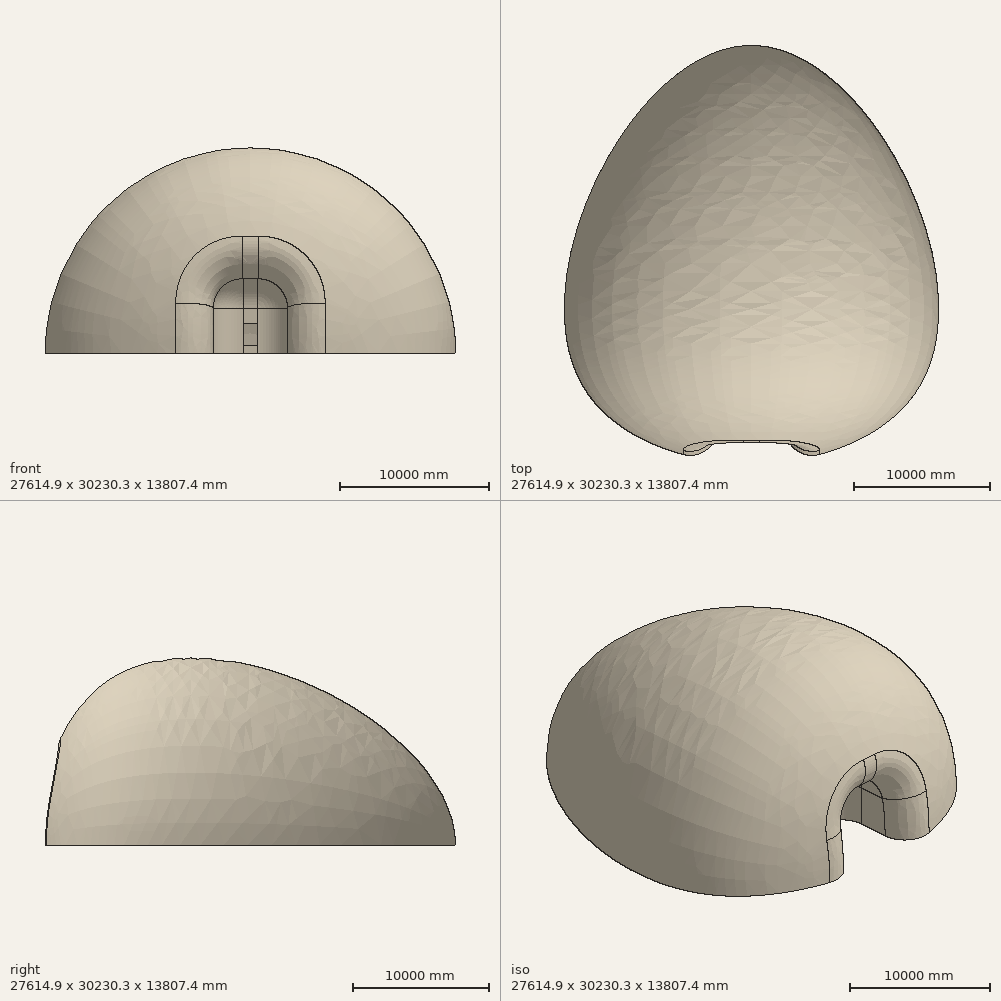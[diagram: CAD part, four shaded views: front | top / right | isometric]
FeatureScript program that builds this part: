
annotation { "Feature Type Name" : "Feature", "Feature Type Description" : "" }
export const myFeature = defineFeature(function(context is Context, id is Id, definition is map)
    precondition{}
    {
        {
            var Q0;
            Q0=qCreatedBy(makeId("Top.planeOp"),FACE);
            var sketch = newSketch(context, id + "F0", { "sketchPlane" : qUnion([Q0])});
            skFitSpline(sketch, "E0", {"points": [v(0, -25000) * mm, v(12500, 0) * mm, v(25000, -25000) * mm, v(0, -25000) * mm]});
            skPoint(sketch, "E1.orphan", {"position": v(0, 0) * mm});
            skPoint(sketch, "E2.orphan", {"position": v(25000, 0) * mm});
            skSolve(sketch);
        }
        {
            var Q0;
            Q0=makeQuery(id+"F0.imprint","IMPRINT",FACE,{"disambiguationData":[TD([[makeQuery(id+"F0.imprint","IMPRINT",EDGE,{"derivedFrom":sQuery(id+"F0.wireOp",EDGE,"E0")}),-1.0]])]});
            var sketch = newSketch(context, id + "F1", { "sketchPlane" : qUnion([Q0])});
            skLineSegment(sketch, "E3", {"start": v(12500, 5000) * mm, "end": v(12500, -35000) * mm});
            skSolve(sketch);
        }
        {
            var Q0;
            {var subQ0=sQuery(id+"F1.wireOp",EDGE,"E3");var subQ1=makeQuery(id+"F0.imprint","IMPRINT",EDGE,{"derivedFrom":sQuery(id+"F0.wireOp",EDGE,"E0")});var subQ2=makeQuery(id+"F1.imprint","INTERSECT",VERTEX,{"disambiguationData":[OD(0.0)],"derivedFrom":[subQ1,subQ0]});Q0=makeQuery(id+"F1.imprint","IMPRINT",FACE,{"disambiguationData":[TD([[makeQuery(id+"F1.imprint","IMPRINT",EDGE,{"disambiguationData":[TD([[subQ2,1.0]])],"derivedFrom":subQ0}),1.0]])]});}
            var Q1;
            Q1=sQuery(id+"F1.wireOp",EDGE,"E3");
            revolve(context, id + "F2", {"entities" : qUnion([Q0]), "axis" : qUnion([Q1]), "revolveType" : RevolveType.FULL});
        }
        {
            var Q0;
            Q0=makeQuery(id+"F0.imprint","IMPRINT",FACE,{"disambiguationData":[TD([[makeQuery(id+"F0.imprint","IMPRINT",EDGE,{"derivedFrom":sQuery(id+"F0.wireOp",EDGE,"E0")}),-1.0]])]});
            extrude(context, id + "F3", {"entities" : qUnion([Q0]), "operationType" : NewBodyOperationType.REMOVE, "oppositeDirection" : true, "depth" : 30000 * mm});
        }
        {
            var Q0;
            Q0=makeQuery(id+"F0.imprint","IMPRINT",FACE,{"disambiguationData":[TD([[makeQuery(id+"F0.imprint","IMPRINT",EDGE,{"derivedFrom":sQuery(id+"F0.wireOp",EDGE,"E0")}),-1.0]])]});
            var sketch = newSketch(context, id + "F4", { "sketchPlane" : qUnion([Q0])});
            skLineSegment(sketch, "E4.bottom", {"start": v(15000, -32000) * mm, "end": v(10000, -32000) * mm});
            skLineSegment(sketch, "E4.top", {"start": v(15000, -23799.97) * mm, "end": v(10000, -23799.97) * mm});
            skLineSegment(sketch, "E4.left", {"start": v(15000, -32000) * mm, "end": v(15000, -23799.97) * mm});
            skLineSegment(sketch, "E4.right", {"start": v(10000, -32000) * mm, "end": v(10000, -23799.97) * mm});
            skSolve(sketch);
        }
        {
            var Q0;
            Q0 = qSketchRegion(id + "F4", true);
            extrude(context, id + "F5", {"entities" : qUnion([Q0]), "operationType" : NewBodyOperationType.REMOVE, "depth" : 5000 * mm});
        }
        {
            var Q0;
            Q0=makeQuery(id+"F5.boolean.opBoolean","COPY",EDGE,{"derivedFrom":makeQuery(id+"F5.opExtrude","SWEPT_EDGE",EDGE,{"disambiguationData":[OSD([sQuery(id+"F4.wireOp",EDGE,"E4.top"),sQuery(id+"F4.wireOp",EDGE,"E4.right")])]})});
            var Q1;
            Q1=makeQuery(id+"F5.boolean.opBoolean","COPY",EDGE,{"derivedFrom":makeQuery(id+"F5.opExtrude","CAP_EDGE",EDGE,{"disambiguationData":[OSD([sQuery(id+"F4.wireOp",EDGE,"E4.top")])],"isStart":false})});
            var Q2;
            Q2=makeQuery(id+"F5.boolean.opBoolean","COPY",EDGE,{"derivedFrom":makeQuery(id+"F5.opExtrude","SWEPT_EDGE",EDGE,{"disambiguationData":[OSD([sQuery(id+"F4.wireOp",EDGE,"E4.top"),sQuery(id+"F4.wireOp",EDGE,"E4.left")])]})});
            var Q3;
            Q3=makeQuery(id+"F5.boolean.opBoolean","COPY",EDGE,{"derivedFrom":makeQuery(id+"F5.opExtrude","CAP_EDGE",EDGE,{"disambiguationData":[OSD([sQuery(id+"F4.wireOp",EDGE,"E4.left")])],"isStart":false})});
            var Q4;
            Q4=makeQuery(id+"F5.boolean.opBoolean","COPY",EDGE,{"derivedFrom":makeQuery(id+"F5.opExtrude","CAP_EDGE",EDGE,{"disambiguationData":[OSD([sQuery(id+"F4.wireOp",EDGE,"E4.right")])],"isStart":false})});
            var Q5;
            Q5=makeQuery(id+"F5.boolean.opBoolean","INTERSECT",EDGE,{"derivedFrom":[makeQuery(id+"F2.opRevolve","SWEPT_FACE",FACE,{"disambiguationData":[OSD([sQuery(id+"F0.wireOp",EDGE,"E0")])]}),makeQuery(id+"F5.opExtrude","SWEPT_FACE",FACE,{"disambiguationData":[OSD([sQuery(id+"F4.wireOp",EDGE,"E4.right")])]})]});
            var Q6;
            Q6=makeQuery(id+"F5.boolean.opBoolean","INTERSECT",EDGE,{"derivedFrom":[makeQuery(id+"F2.opRevolve","SWEPT_FACE",FACE,{"disambiguationData":[OSD([sQuery(id+"F0.wireOp",EDGE,"E0")])]}),makeQuery(id+"F5.opExtrude","CAP_FACE",FACE,{"disambiguationData":[OSD([sQuery(id+"F4.wireOp",EDGE,"E4.bottom"),sQuery(id+"F4.wireOp",EDGE,"E4.top"),sQuery(id+"F4.wireOp",EDGE,"E4.left"),sQuery(id+"F4.wireOp",EDGE,"E4.right")])],"isStart":false})]});
            var Q7;
            Q7=makeQuery(id+"F5.boolean.opBoolean","INTERSECT",EDGE,{"derivedFrom":[makeQuery(id+"F2.opRevolve","SWEPT_FACE",FACE,{"disambiguationData":[OSD([sQuery(id+"F0.wireOp",EDGE,"E0")])]}),makeQuery(id+"F5.opExtrude","SWEPT_FACE",FACE,{"disambiguationData":[OSD([sQuery(id+"F4.wireOp",EDGE,"E4.left")])]})]});
            fillet(context, id + "F6", {"entities" : qUnion([Q0, Q1, Q2, Q3, Q4, Q5, Q6, Q7]), "radius" : 2000 * mm, "tangentPropagation" : true, "allowEdgeOverflow" : false});
        }
        {
            var Q0;
            Q0=makeQuery(id+"F2.opRevolve","SWEPT_FACE",FACE,{"disambiguationData":[OSD([sQuery(id+"F0.wireOp",EDGE,"E0")])]});
            var Q1;
            Q1=makeQuery(id+"F6.opFillet","BLEND_FACE",FACE,{"disambiguationData":[OSD([sQuery(id+"F0.wireOp",EDGE,"E0"),sQuery(id+"F4.wireOp",EDGE,"E4.left")])]});
            var Q2;
            {var subQ0=sQuery(id+"F4.wireOp",EDGE,"E4.right");var subQ1=sQuery(id+"F4.wireOp",EDGE,"E4.top");Q2=makeQuery(id+"F6.opFillet","BLEND_FACE",FACE,{"disambiguationData":[OSD([subQ1,subQ0]),TDD([makeQuery(id+"F5.boolean.opBoolean","COPY",EDGE,{"derivedFrom":makeQuery(id+"F5.opExtrude","SWEPT_EDGE",EDGE,{"disambiguationData":[OSD([subQ1,subQ0])]})})])]});}
            var Q3;
            {var subQ0=sQuery(id+"F4.wireOp",EDGE,"E4.right");var subQ1=sQuery(id+"F4.wireOp",EDGE,"E4.left");var subQ2=sQuery(id+"F4.wireOp",EDGE,"E4.top");var subQ3=sQuery(id+"F4.wireOp",EDGE,"E4.bottom");var subQ4=sQuery(id+"F0.wireOp",EDGE,"E0");Q3=makeQuery(id+"F6.opFillet","BLEND_FACE",FACE,{"disambiguationData":[OSD([subQ4,subQ3,subQ2,subQ1,subQ0]),TDD([makeQuery(id+"F5.boolean.opBoolean","INTERSECT",VERTEX,{"derivedFrom":[makeQuery(id+"F2.opRevolve","SWEPT_FACE",FACE,{"disambiguationData":[OSD([subQ4])]}),makeQuery(id+"F5.opExtrude","CAP_FACE",FACE,{"disambiguationData":[OSD([subQ3,subQ2,subQ1,subQ0])],"isStart":false}),makeQuery(id+"F5.opExtrude","SWEPT_FACE",FACE,{"disambiguationData":[OSD([subQ0])]})]})])]});}
            var Q4;
            {var subQ0=sQuery(id+"F4.wireOp",EDGE,"E4.left");var subQ1=sQuery(id+"F4.wireOp",EDGE,"E4.top");Q4=makeQuery(id+"F6.opFillet","BLEND_FACE",FACE,{"disambiguationData":[OSD([subQ1,subQ0]),TDD([makeQuery(id+"F5.boolean.opBoolean","COPY",EDGE,{"derivedFrom":makeQuery(id+"F5.opExtrude","SWEPT_EDGE",EDGE,{"disambiguationData":[OSD([subQ1,subQ0])]})})])]});}
            var Q5;
            {var subQ0=sQuery(id+"F4.wireOp",EDGE,"E4.left");var subQ1=sQuery(id+"F4.wireOp",EDGE,"E4.right");var subQ2=sQuery(id+"F4.wireOp",EDGE,"E4.top");var subQ3=sQuery(id+"F4.wireOp",EDGE,"E4.bottom");var subQ4=sQuery(id+"F0.wireOp",EDGE,"E0");Q5=makeQuery(id+"F6.opFillet","BLEND_FACE",FACE,{"disambiguationData":[OSD([subQ4,subQ3,subQ2,subQ0,subQ1]),TDD([makeQuery(id+"F5.boolean.opBoolean","INTERSECT",VERTEX,{"derivedFrom":[makeQuery(id+"F2.opRevolve","SWEPT_FACE",FACE,{"disambiguationData":[OSD([subQ4])]}),makeQuery(id+"F5.opExtrude","CAP_FACE",FACE,{"disambiguationData":[OSD([subQ3,subQ2,subQ0,subQ1])],"isStart":false}),makeQuery(id+"F5.opExtrude","SWEPT_FACE",FACE,{"disambiguationData":[OSD([subQ0])]})]})])]});}
            var Q6;
            {var subQ0=sQuery(id+"F4.wireOp",EDGE,"E4.right");var subQ1=sQuery(id+"F4.wireOp",EDGE,"E4.left");var subQ2=sQuery(id+"F4.wireOp",EDGE,"E4.top");var subQ3=sQuery(id+"F4.wireOp",EDGE,"E4.bottom");var subQ4=sQuery(id+"F0.wireOp",EDGE,"E0");Q6=makeQuery(id+"F6.opFillet","BLEND_FACE",FACE,{"disambiguationData":[OSD([subQ4,subQ3,subQ2,subQ1,subQ0]),TDD([makeQuery(id+"F5.boolean.opBoolean","INTERSECT",EDGE,{"derivedFrom":[makeQuery(id+"F2.opRevolve","SWEPT_FACE",FACE,{"disambiguationData":[OSD([subQ4])]}),makeQuery(id+"F5.opExtrude","CAP_FACE",FACE,{"disambiguationData":[OSD([subQ3,subQ2,subQ1,subQ0])],"isStart":false})]})])]});}
            var Q7;
            Q7=makeQuery(id+"F6.opFillet","BLEND_FACE",FACE,{"disambiguationData":[OSD([sQuery(id+"F0.wireOp",EDGE,"E0"),sQuery(id+"F4.wireOp",EDGE,"E4.right")])]});
            var Q8;
            {var subQ0=sQuery(id+"F4.wireOp",EDGE,"E4.right");var subQ1=sQuery(id+"F4.wireOp",EDGE,"E4.top");Q8=makeQuery(id+"F6.opFillet","BLEND_FACE",FACE,{"disambiguationData":[OSD([subQ1,subQ0]),TDD([makeQuery(id+"F5.boolean.opBoolean","COPY",VERTEX,{"derivedFrom":makeQuery(id+"F5.opExtrude","CAP_VERTEX",VERTEX,{"disambiguationData":[OSD([subQ1,subQ0])],"isStart":false})})])]});}
            var Q9;
            Q9=makeQuery(id+"F5.boolean.opBoolean","COPY",FACE,{"derivedFrom":makeQuery(id+"F5.opExtrude","SWEPT_FACE",FACE,{"disambiguationData":[OSD([sQuery(id+"F4.wireOp",EDGE,"E4.right")])]})});
            var Q10;
            Q10=makeQuery(id+"F6.opFillet","BLEND_FACE",FACE,{"disambiguationData":[OSD([sQuery(id+"F4.wireOp",EDGE,"E4.top")])]});
            var Q11;
            Q11=makeQuery(id+"F5.boolean.opBoolean","COPY",FACE,{"derivedFrom":makeQuery(id+"F5.opExtrude","CAP_FACE",FACE,{"disambiguationData":[OSD([sQuery(id+"F4.wireOp",EDGE,"E4.bottom"),sQuery(id+"F4.wireOp",EDGE,"E4.top"),sQuery(id+"F4.wireOp",EDGE,"E4.left"),sQuery(id+"F4.wireOp",EDGE,"E4.right")])],"isStart":false})});
            var Q12;
            Q12=makeQuery(id+"F6.opFillet","BLEND_FACE",FACE,{"disambiguationData":[OSD([sQuery(id+"F4.wireOp",EDGE,"E4.right")])]});
            var Q13;
            Q13=makeQuery(id+"F6.opFillet","BLEND_FACE",FACE,{"disambiguationData":[OSD([sQuery(id+"F4.wireOp",EDGE,"E4.left")])]});
            var Q14;
            {var subQ0=sQuery(id+"F4.wireOp",EDGE,"E4.left");var subQ1=sQuery(id+"F4.wireOp",EDGE,"E4.top");Q14=makeQuery(id+"F6.opFillet","BLEND_FACE",FACE,{"disambiguationData":[OSD([subQ1,subQ0]),TDD([makeQuery(id+"F5.boolean.opBoolean","COPY",VERTEX,{"derivedFrom":makeQuery(id+"F5.opExtrude","CAP_VERTEX",VERTEX,{"disambiguationData":[OSD([subQ1,subQ0])],"isStart":false})})])]});}
            var Q15;
            Q15=makeQuery(id+"F5.boolean.opBoolean","COPY",FACE,{"derivedFrom":makeQuery(id+"F5.opExtrude","SWEPT_FACE",FACE,{"disambiguationData":[OSD([sQuery(id+"F4.wireOp",EDGE,"E4.top")])]})});
            var Q16;
            Q16=makeQuery(id+"F5.boolean.opBoolean","COPY",FACE,{"derivedFrom":makeQuery(id+"F5.opExtrude","SWEPT_FACE",FACE,{"disambiguationData":[OSD([sQuery(id+"F4.wireOp",EDGE,"E4.left")])]})});
            var Q17;
            Q17=makeQuery(id+"F2.opRevolve","SWEPT_BODY",BODY,{"disambiguationData":[OSD([sQuery(id+"F0.wireOp",EDGE,"E0"),sQuery(id+"F1.wireOp",EDGE,"E3")])]});
            shell(context, id + "F7", {"isHollow" : true, "entities" : qUnion([Q0, Q1, Q2, Q3, Q4, Q5, Q6, Q7, Q8, Q9, Q10, Q11, Q12, Q13, Q14, Q15, Q16]), "parts" : qUnion([Q17]), "thickness" : 500 * mm});
        }
        {
            var Q0;
            Q0=makeQuery(id+"F5.boolean.opBoolean","COPY",FACE,{"derivedFrom":makeQuery(id+"F5.opExtrude","SWEPT_FACE",FACE,{"disambiguationData":[OSD([sQuery(id+"F4.wireOp",EDGE,"E4.top")])]})});
            var sketch = newSketch(context, id + "F8", { "sketchPlane" : qUnion([Q0])});
            skLineSegment(sketch, "E5.top", {"start": v(13000, 2000) * mm, "end": v(12000, 2000) * mm});
            skLineSegment(sketch, "E5.left", {"start": v(13000, 500) * mm, "end": v(13000, 2000) * mm});
            skLineSegment(sketch, "E5.right", {"start": v(12000, 500) * mm, "end": v(12000, 2000) * mm});
            skLineSegment(sketch, "E6.top", {"start": v(13000, 500) * mm, "end": v(12000, 500) * mm});
            skSolve(sketch);
        }
        {
            var Q0;
            Q0=makeQuery(id+"F8.imprint","IMPRINT",FACE,{"disambiguationData":[TD([[makeQuery(id+"F8.imprint","IMPRINT",EDGE,{"derivedFrom":sQuery(id+"F8.wireOp",EDGE,"E5.top")}),1.0]])]});
            extrude(context, id + "F9", {"entities" : qUnion([Q0]), "operationType" : NewBodyOperationType.REMOVE, "oppositeDirection" : true, "depth" : 1000 * mm});
        }
    });
